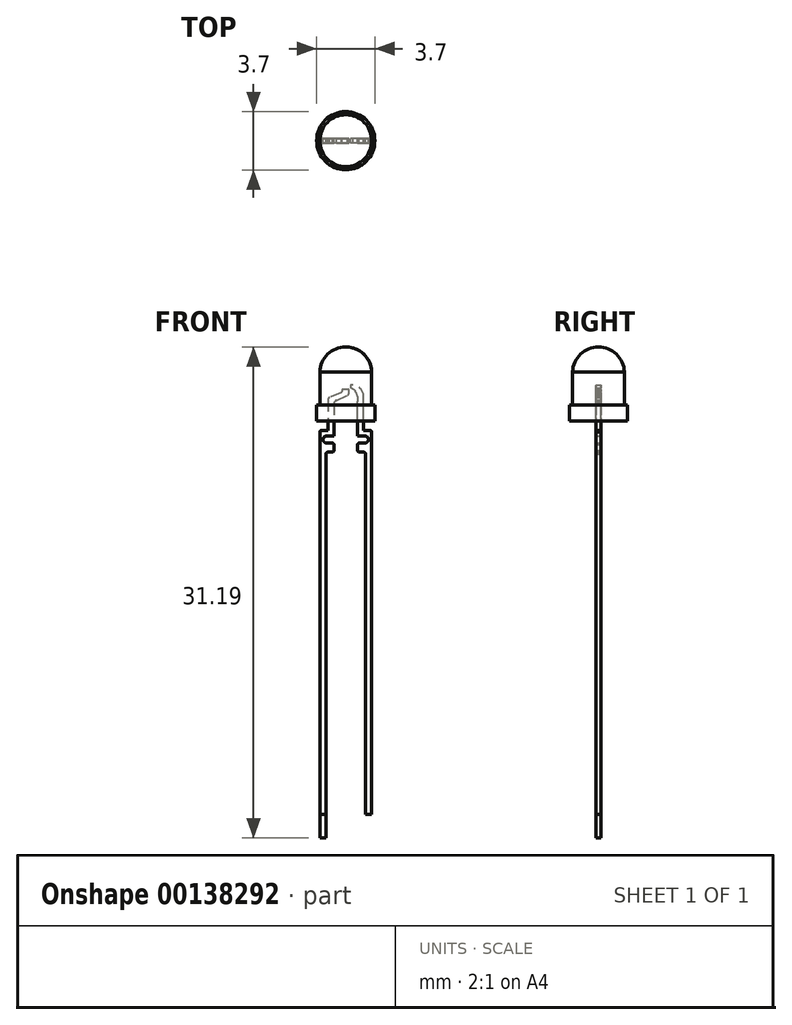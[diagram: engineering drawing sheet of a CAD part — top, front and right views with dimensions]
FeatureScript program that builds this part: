
annotation { "Feature Type Name" : "Feature", "Feature Type Description" : "" }
export const myFeature = defineFeature(function(context is Context, id is Id, definition is map)
    precondition{}
    {
        {
            var Q0;
            Q0=qCreatedBy(makeId("Front.planeOp"),FACE);
            var sketch = newSketch(context, id + "F0", { "sketchPlane" : qUnion([Q0])});
            skLineSegment(sketch, "E0.bottom", {"start": v(0, 0.5) * mm, "end": v(-1.85, 0.5) * mm});
            skLineSegment(sketch, "E0.top", {"start": v(0, -0.5) * mm, "end": v(-1.85, -0.5) * mm});
            skLineSegment(sketch, "E0.right", {"start": v(-1.85, 0.5) * mm, "end": v(-1.85, -0.5) * mm});
            skPoint(sketch, "E0.middle", {"position": v(0, 0) * mm});
            skLineSegment(sketch, "E1", {"start": v(0, -0.5) * mm, "end": v(0, 2.55) * mm});
            skPoint(sketch, "E1.endSnap0", {"position": v(0, 0.5) * mm});
            skArc(sketch, "E2", {"start": v(0, 4.2) * mm, "mid": v(-1.19, 3.7) * mm, "end": v(-1.65, 2.49) * mm});
            skLineSegment(sketch, "E3", {"start": v(-1.65, 2.61) * mm, "end": v(-1.65, 0.5) * mm});
            skLineSegment(sketch, "E4", {"start": v(0, 2.55) * mm, "end": v(0, 4.2) * mm});
            skPoint(sketch, "E0.left.start.orphan", {"position": v(1.85, 0.5) * mm});
            skPoint(sketch, "E5.orphan", {"position": v(1.85, -0.5) * mm});
            skSolve(sketch);
        }
        {
            var Q0;
            {var subQ4=sQuery(id+"F0.wireOp",EDGE,"E4");Q0=makeQuery(id+"F0.imprint","IMPRINT",FACE,{"disambiguationData":[TD([[makeQuery(id+"F0.imprint","IMPRINT",EDGE,{"derivedFrom":subQ4}),1.0]])]});}
            var Q1;
            {var subQ1=sQuery(id+"F0.wireOp",EDGE,"E0.top");Q1=makeQuery(id+"F0.imprint","IMPRINT",FACE,{"disambiguationData":[TD([[makeQuery(id+"F0.imprint","IMPRINT",EDGE,{"derivedFrom":subQ1}),-1.0]])]});}
            var Q2;
            Q2=sQuery(id+"F0.wireOp",EDGE,"E1");
            revolve(context, id + "F1", {"entities" : qUnion([Q0, Q1]), "axis" : qUnion([Q2]), "revolveType" : RevolveType.FULL});
        }
        {
            var Q0;
            Q0=qCreatedBy(makeId("Front.planeOp"),FACE);
            var sketch = newSketch(context, id + "F2", { "sketchPlane" : qUnion([Q0])});
            skLineSegment(sketch, "E6", {"start": v(0, 0) * mm, "end": v(0, -5.55) * mm, "construction": true});
            skLineSegment(sketch, "E7", {"start": v(-0.75, -0.7) * mm, "end": v(-0.75, -1.46) * mm});
            skLineSegment(sketch, "E8", {"start": v(-0.75, -1.46) * mm, "end": v(-1.24, -1.46) * mm});
            skLineSegment(sketch, "E9", {"start": v(-1.23, -1.9) * mm, "end": v(-0.85, -1.9) * mm});
            skLineSegment(sketch, "E10", {"start": v(-0.75, -2) * mm, "end": v(-0.75, -2.39) * mm});
            skLineSegment(sketch, "E11", {"start": v(-0.85, -2.48) * mm, "end": v(-1.15, -2.48) * mm});
            skLineSegment(sketch, "E12", {"start": v(-1.27, -2.6) * mm, "end": v(-1.27, -25.48) * mm});
            skLineSegment(sketch, "E13", {"start": v(-1.27, -25.48) * mm, "end": v(-1.64, -25.48) * mm});
            skLineSegment(sketch, "E14", {"start": v(-1.64, -25.48) * mm, "end": v(-1.64, -1.2) * mm});
            skLineSegment(sketch, "E15", {"start": v(-1.53, -1.1) * mm, "end": v(-1.14, -1.1) * mm});
            skLineSegment(sketch, "E16", {"start": v(-1.14, -1.1) * mm, "end": v(-1.14, -0.7) * mm});
            skArc(sketch, "E17", {"start": v(-1.24, -1.46) * mm, "mid": v(-1.44, -1.68) * mm, "end": v(-1.23, -1.9) * mm});
            skArc(sketch, "E18", {"start": v(-0.75, -2) * mm, "mid": v(-0.79, -1.93) * mm, "end": v(-0.85, -1.9) * mm});
            skArc(sketch, "E19", {"start": v(-0.85, -2.48) * mm, "mid": v(-0.79, -2.45) * mm, "end": v(-0.75, -2.39) * mm});
            skArc(sketch, "E20", {"start": v(-1.15, -2.48) * mm, "mid": v(-1.23, -2.52) * mm, "end": v(-1.27, -2.6) * mm});
            skArc(sketch, "E21", {"start": v(-1.53, -1.1) * mm, "mid": v(-1.6, -1.13) * mm, "end": v(-1.64, -1.2) * mm});
            skLineSegment(sketch, "E22.MirrorCS", {"start": v(1.14, -1.1) * mm, "end": v(1.14, -0.7) * mm});
            skLineSegment(sketch, "E23.MirrorCS", {"start": v(0.75, -0.7) * mm, "end": v(0.75, -1.46) * mm});
            skArc(sketch, "E24.MirrorCS", {"start": v(1.15, -2.48) * mm, "mid": v(1.23, -2.52) * mm, "end": v(1.27, -2.6) * mm});
            skArc(sketch, "E25.MirrorCS", {"start": v(1.53, -1.1) * mm, "mid": v(1.6, -1.13) * mm, "end": v(1.64, -1.2) * mm});
            skArc(sketch, "E26.MirrorCS", {"start": v(0.75, -2) * mm, "mid": v(0.79, -1.93) * mm, "end": v(0.85, -1.9) * mm});
            skArc(sketch, "E27.MirrorCS", {"start": v(0.85, -2.48) * mm, "mid": v(0.79, -2.45) * mm, "end": v(0.75, -2.39) * mm});
            skLineSegment(sketch, "E28.MirrorCS", {"start": v(0.85, -2.48) * mm, "end": v(1.15, -2.48) * mm});
            skLineSegment(sketch, "E29.MirrorCS", {"start": v(1.27, -2.6) * mm, "end": v(1.27, -25.48) * mm});
            skLineSegment(sketch, "E30.MirrorCS", {"start": v(0.75, -2) * mm, "end": v(0.75, -2.39) * mm});
            skLineSegment(sketch, "E31.MirrorCS", {"start": v(1.27, -25.48) * mm, "end": v(1.64, -25.48) * mm});
            skLineSegment(sketch, "E32.MirrorCS", {"start": v(0.75, -1.46) * mm, "end": v(1.24, -1.46) * mm});
            skLineSegment(sketch, "E33.MirrorCS", {"start": v(1.64, -25.48) * mm, "end": v(1.64, -1.2) * mm});
            skLineSegment(sketch, "E34.MirrorCS", {"start": v(1.23, -1.9) * mm, "end": v(0.85, -1.9) * mm});
            skLineSegment(sketch, "E35.MirrorCS", {"start": v(1.53, -1.1) * mm, "end": v(1.14, -1.1) * mm});
            skArc(sketch, "E36.MirrorCS", {"start": v(1.24, -1.46) * mm, "mid": v(1.44, -1.68) * mm, "end": v(1.23, -1.9) * mm});
            skLineSegment(sketch, "E37", {"start": v(-0.75, -0.7) * mm, "end": v(-0.75, 0.64) * mm});
            skLineSegment(sketch, "E38", {"start": v(-1.14, -0.7) * mm, "end": v(-1.14, 0.72) * mm});
            skLineSegment(sketch, "E39", {"start": v(0.75, -0.7) * mm, "end": v(0.75, 0.75) * mm});
            skLineSegment(sketch, "E40", {"start": v(1.14, -0.7) * mm, "end": v(1.14, 0.74) * mm});
            skLineSegment(sketch, "E41", {"start": v(-0.6, 0.81) * mm, "end": v(0.14, 1.15) * mm});
            skLineSegment(sketch, "E42", {"start": v(0.2, 1.23) * mm, "end": v(0.2, 1.5) * mm});
            skLineSegment(sketch, "E43", {"start": v(0.2, 1.5) * mm, "end": v(-0.23, 1.5) * mm});
            skLineSegment(sketch, "E44", {"start": v(-0.23, 1.5) * mm, "end": v(-0.23, 1.38) * mm});
            skLineSegment(sketch, "E45", {"start": v(-0.27, 1.31) * mm, "end": v(-1.03, 1) * mm});
            skLineSegment(sketch, "E46", {"start": v(-1.14, 0.84) * mm, "end": v(-1.14, 0.72) * mm});
            skArc(sketch, "E47", {"start": v(-0.6, 0.81) * mm, "mid": v(-0.69, 0.73) * mm, "end": v(-0.75, 0.64) * mm});
            skArc(sketch, "E48", {"start": v(-1.03, 1) * mm, "mid": v(-1.1, 0.93) * mm, "end": v(-1.14, 0.84) * mm});
            skArc(sketch, "E49", {"start": v(-0.27, 1.31) * mm, "mid": v(-0.23, 1.36) * mm, "end": v(-0.23, 1.41) * mm});
            skArc(sketch, "E50", {"start": v(0.1, 1.13) * mm, "mid": v(0.16, 1.17) * mm, "end": v(0.2, 1.23) * mm});
            skPoint(sketch, "E51.orphan", {"position": v(-1.14, 0.96) * mm});
            skPoint(sketch, "E52.orphan", {"position": v(0.2, 1.18) * mm});
            skPoint(sketch, "E53.orphan", {"position": v(0.2, 1.34) * mm});
            skPoint(sketch, "E54.orphan", {"position": v(-0.23, 1.33) * mm});
            skLineSegment(sketch, "E55", {"start": v(0.75, -1.46) * mm, "end": v(1.14, -1.1) * mm});
            skLineSegment(sketch, "E56", {"start": v(0.75, 0.75) * mm, "end": v(1.14, 0.74) * mm});
            skLineSegment(sketch, "E57", {"start": v(1.14, 0.74) * mm, "end": v(1.14, 1.06) * mm});
            skLineSegment(sketch, "E58", {"start": v(0.47, 1.8) * mm, "end": v(0.3, 1.8) * mm});
            skLineSegment(sketch, "E59", {"start": v(0.3, 1.8) * mm, "end": v(0.3, 1.6) * mm});
            skLineSegment(sketch, "E60", {"start": v(0.74, 1.05) * mm, "end": v(0.75, 0.75) * mm});
            skArc(sketch, "E61", {"start": v(0.74, 0.98) * mm, "mid": v(0.63, 1.36) * mm, "end": v(0.3, 1.6) * mm});
            skArc(sketch, "E62", {"start": v(1.14, 0.99) * mm, "mid": v(0.96, 1.52) * mm, "end": v(0.47, 1.8) * mm});
            skSolve(sketch);
        }
        {
            var Q0;
            Q0=qCreatedBy(makeId("Front.planeOp"),FACE);
            var sketch = newSketch(context, id + "F3", { "sketchPlane" : qUnion([Q0])});
            skLineSegment(sketch, "E63", {"start": v(-1.64, -25.49) * mm, "end": v(-1.64, -26.99) * mm});
            skLineSegment(sketch, "E64", {"start": v(-1.64, -26.99) * mm, "end": v(-1.27, -26.99) * mm});
            skLineSegment(sketch, "E65", {"start": v(-1.27, -26.99) * mm, "end": v(-1.27, -25.49) * mm});
            skLineSegment(sketch, "E66", {"start": v(-1.27, -25.49) * mm, "end": v(-1.64, -25.49) * mm});
            skSolve(sketch);
        }
        {
            var Q0;
            Q0 = qSketchRegion(id + "F2", true);
            var Q1;
            Q1=makeQuery(id+"F3.imprint","IMPRINT",FACE,{"disambiguationData":[TD([[makeQuery(id+"F3.imprint","IMPRINT",EDGE,{"derivedFrom":sQuery(id+"F3.wireOp",EDGE,"E63")}),1.0]])]});
            extrude(context, id + "F4", {"entities" : qUnion([Q0, Q1]), "endBound" : BoundingType.SYMMETRIC, "depth" : .3 * mm});
        }
    });
